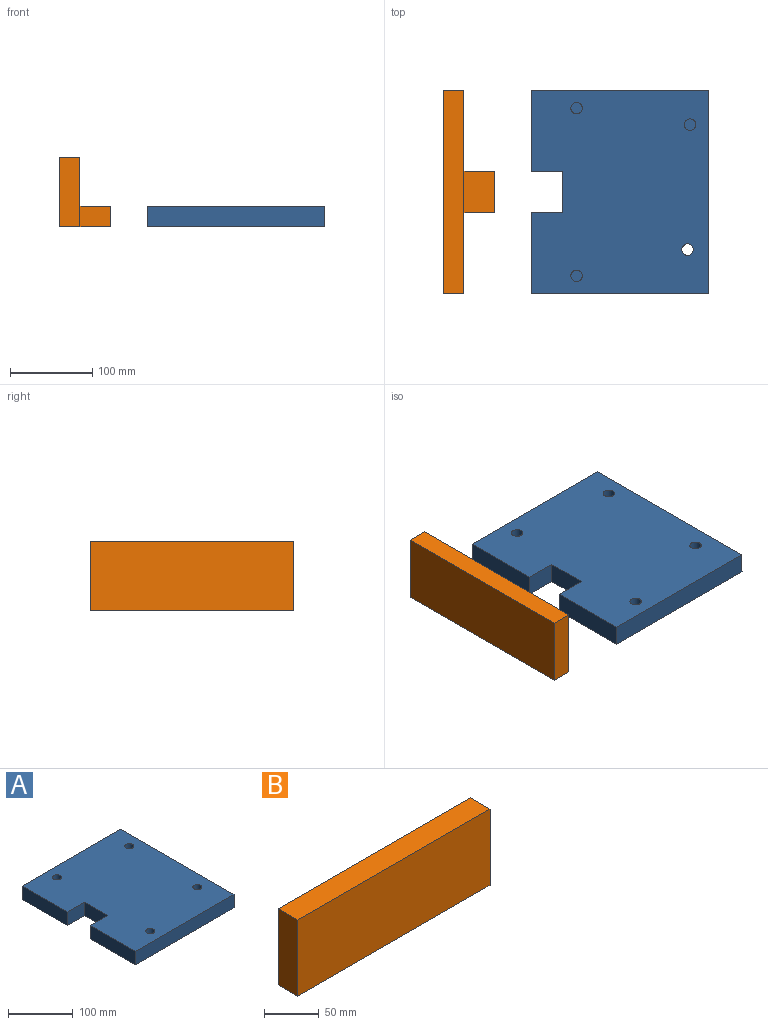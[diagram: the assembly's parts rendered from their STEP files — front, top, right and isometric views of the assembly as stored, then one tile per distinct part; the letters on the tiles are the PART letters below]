
ASSEMBLY  parts=2 mates=1
PART A: 17 faces, bbox 216x248x25.4 mm
  f0: plane 98.6x25.4mm, normal (-1,0,0), area 2504.4mm2, adj f1,f3,f6,f14
  f1: plane 248x216mm, normal (0,0,-1), area 51483.7mm2, adj f0,f2,f4,f5,f6,f11,f14,f15
  f2: plane 248x25.4mm, normal (1,0,0), area 6299.2mm2, adj f1,f3,f5,f6
  f3: plane 248x216mm, normal (0,0,1), area 51021.8mm2, adj f0,f2,f4,f5,f6,f7,f9,f11
  f4: plane 98.6x25.4mm, normal (-1,0,0), area 2504.4mm2, adj f1,f3,f5,f16
  f5: plane 216x25.4mm, normal (0,1,0), area 5486.4mm2, adj f1,f2,f3,f4
  f6: plane 216x25.4mm, normal (0,-1,0), area 5486.4mm2, adj f0,f1,f2,f3
  f7: cylinder r=7mm len=14mm, axis (0,0,1), area 558.6mm2, adj f3,f8
  f8: plane 14x14mm, normal (0,0,1), area 153.9mm2, adj f7
  f9: cylinder r=7mm len=14mm, axis (0,0,1), area 558.6mm2, adj f3,f10
  f10: plane 14x14mm, normal (0,0,1), area 153.9mm2, adj f9
  f11: cylinder r=7mm len=25.4mm, axis (0,0,1), area 1117.2mm2, adj f1,f3
  f12: cylinder r=7mm len=14mm, axis (0,0,1), area 558.6mm2, adj f3,f13
  f13: plane 14x14mm, normal (0,0,1), area 153.9mm2, adj f12
  f14: plane 38x25.4mm, normal (0,1,0), area 965.2mm2, adj f0,f1,f3,f15
  f15: plane 50.8x25.4mm, normal (-1,0,0), area 1290.3mm2, adj f1,f3,f14,f16
  f16: plane 38x25.4mm, normal (0,-1,0), area 965.2mm2, adj f1,f3,f4,f15
PART B: 14 faces, bbox 248x62.9x85 mm
  f0: plane 85x25.4mm, normal (-1,0,0), area 2159mm2, adj f1,f3,f4,f5
  f1: plane 248x62.9mm, normal (0,0,-1), area 8189.2mm2, adj f0,f2,f4,f5,f6,f8,f9
  f2: plane 85x25.4mm, normal (1,0,0), area 2159mm2, adj f1,f3,f4,f5
  f3: plane 248x25.4mm, normal (0,0,1), area 6299.2mm2, adj f0,f2,f4,f5
  f4: plane 248x85mm, normal (0,-1,0), area 21080mm2, adj f0,f1,f2,f3
  f5: plane 248x85mm, normal (0,1,0), area 19502mm2, adj f0,f1,f2,f3,f6,f7,f8,f10
  f6: plane 37.5x25.2mm, normal (1,0,0), area 945mm2, adj f1,f5,f7,f9
  f7: plane 50.4x37.5mm, normal (0,0,1), area 1890mm2, adj f5,f6,f8,f9
  f8: plane 37.5x25.2mm, normal (-1,0,0), area 945mm2, adj f1,f5,f7,f9
  f9: plane 50.4x25.2mm, normal (0,1,0), area 1270.1mm2, adj f1,f6,f7,f8
  f10: cylinder r=7mm len=14mm, axis (0,1,0), area 558.6mm2, adj f5,f11
  f11: plane 14x14mm, normal (0,1,0), area 153.9mm2, adj f10
  f12: cylinder r=7mm len=14mm, axis (0,1,0), area 558.6mm2, adj f5,f13
  f13: plane 14x14mm, normal (0,1,0), area 153.9mm2, adj f12
PLACE A t=(-329.07,-64.09,-62.81)mm fixed
PLACE B rot(axis=(0,0,-1),90deg) t=(-627.16,183.91,-62.71)mm
MATE slider B.f9 <-> A.f15  axis (1,0,0) through (-589.66,59.91,-50.11)mm
